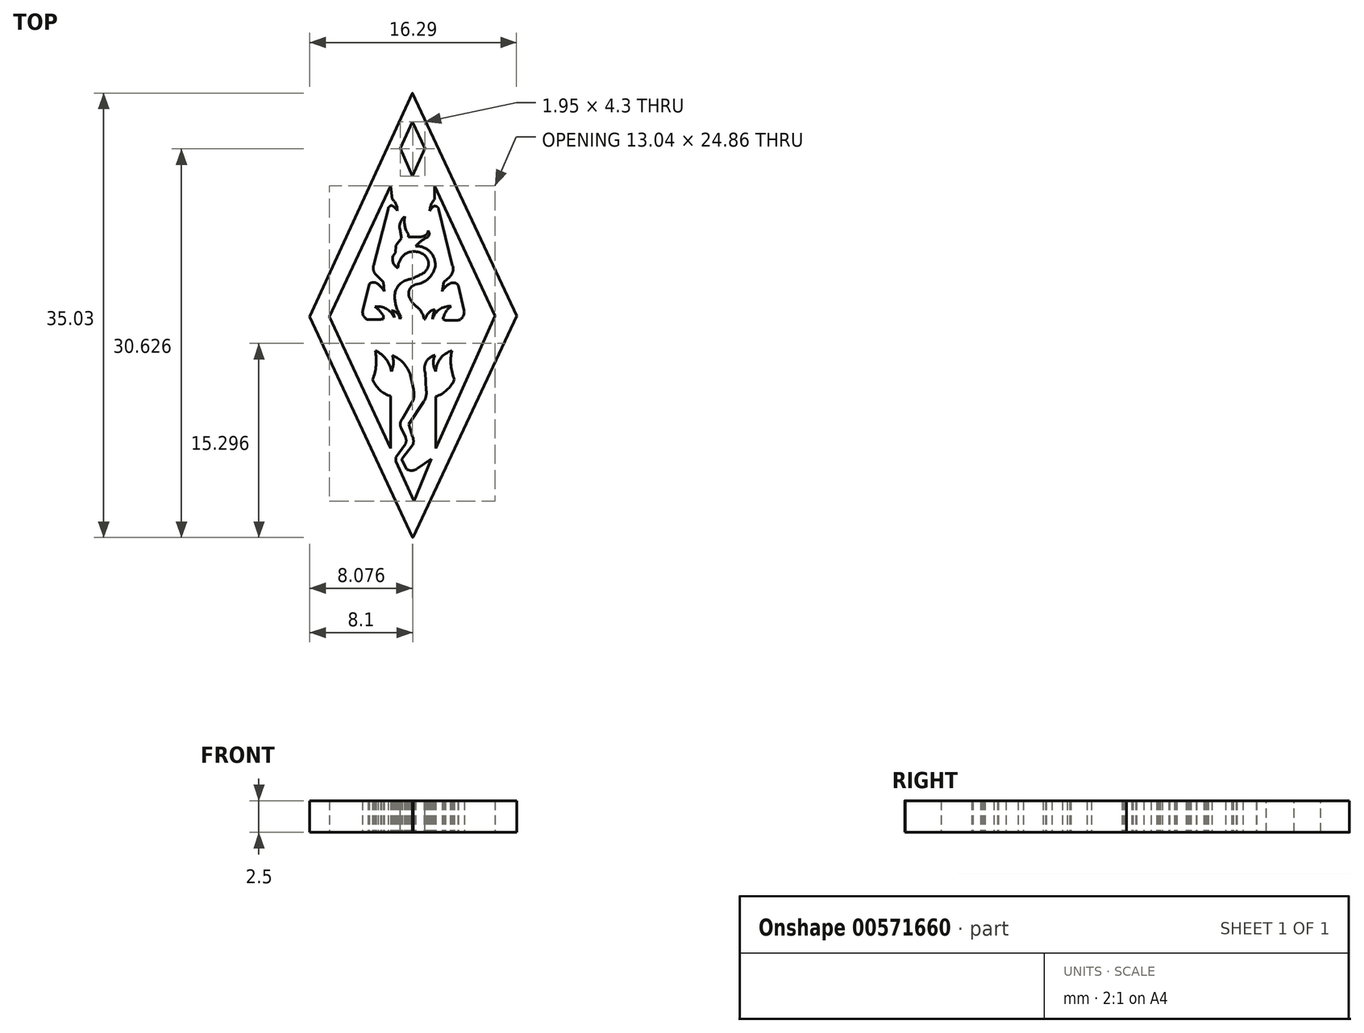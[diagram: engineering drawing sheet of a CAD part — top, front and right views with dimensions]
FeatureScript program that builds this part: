
annotation { "Feature Type Name" : "Feature", "Feature Type Description" : "" }
export const myFeature = defineFeature(function(context is Context, id is Id, definition is map)
    precondition{}
    {
        {
            var Q0;
            Q0=qCreatedBy(makeId("Top.planeOp"),FACE);
            var sketch = newSketch(context, id + "F0", { "sketchPlane" : qUnion([Q0])});
            skPoint(sketch, "E0.endSnap0", {"position": v(12.98, 25.96) * mm});
            skLineSegment(sketch, "E1", {"start": v(14.47, 3.72) * mm, "end": v(13.1, 0.4) * mm});
            skLineSegment(sketch, "E2", {"start": v(13.1, 0.4) * mm, "end": v(11.67, 3.52) * mm});
            skLineSegment(sketch, "E3", {"start": v(14.47, 3.72) * mm, "end": v(13.35, 2.95) * mm});
            skLineSegment(sketch, "E4", {"start": v(12.54, 2.9) * mm, "end": v(12.14, 3.64) * mm});
            skArc(sketch, "E5", {"start": v(12.54, 2.9) * mm, "mid": v(12.95, 2.8) * mm, "end": v(13.35, 2.95) * mm});
            skLineSegment(sketch, "E6", {"start": v(11.67, 3.52) * mm, "end": v(11.67, 3.85) * mm});
            skLineSegment(sketch, "E7", {"start": v(12.14, 3.64) * mm, "end": v(12.14, 3.7) * mm});
            skLineSegment(sketch, "E8", {"start": v(12.14, 3.7) * mm, "end": v(13.02, 4.84) * mm});
            skLineSegment(sketch, "E9", {"start": v(11.67, 3.85) * mm, "end": v(12.44, 4.91) * mm});
            skArc(sketch, "E10", {"start": v(13.02, 4.84) * mm, "mid": v(13.05, 5.18) * mm, "end": v(12.99, 5.51) * mm});
            skLineSegment(sketch, "E11", {"start": v(12.42, 5.44) * mm, "end": v(12.08, 6.18) * mm});
            skArc(sketch, "E12", {"start": v(12.44, 4.91) * mm, "mid": v(12.48, 5.18) * mm, "end": v(12.42, 5.44) * mm});
            skLineSegment(sketch, "E13", {"start": v(12.17, 6.88) * mm, "end": v(13.06, 8.42) * mm});
            skArc(sketch, "E14", {"start": v(12.17, 6.88) * mm, "mid": v(12.02, 6.54) * mm, "end": v(12.08, 6.18) * mm});
            skLineSegment(sketch, "E15", {"start": v(12.99, 5.51) * mm, "end": v(12.68, 6.46) * mm});
            skLineSegment(sketch, "E16", {"start": v(12.68, 6.46) * mm, "end": v(13.87, 8.24) * mm});
            skArc(sketch, "E17", {"start": v(13.87, 8.24) * mm, "mid": v(14.05, 8.66) * mm, "end": v(14.06, 9.12) * mm});
            skArc(sketch, "E18", {"start": v(13.06, 8.42) * mm, "mid": v(13.1, 8.8) * mm, "end": v(13.06, 9.19) * mm});
            skLineSegment(sketch, "E19", {"start": v(13.06, 9.19) * mm, "end": v(12.81, 10.33) * mm});
            skLineSegment(sketch, "E20", {"start": v(14.06, 9.12) * mm, "end": v(13.98, 10.53) * mm});
            skArc(sketch, "E21", {"start": v(12.81, 10.33) * mm, "mid": v(12.28, 11.27) * mm, "end": v(11.39, 11.89) * mm});
            skArc(sketch, "E22", {"start": v(11.3, 10.61) * mm, "mid": v(11.47, 11.24) * mm, "end": v(11.39, 11.89) * mm});
            skArc(sketch, "E23", {"start": v(11.3, 10.61) * mm, "mid": v(10.9, 11.6) * mm, "end": v(10.05, 12.26) * mm});
            skArc(sketch, "E24", {"start": v(9.83, 9.97) * mm, "mid": v(10.1, 11.1) * mm, "end": v(10.05, 12.26) * mm});
            skArc(sketch, "E25", {"start": v(9.83, 9.97) * mm, "mid": v(10.4, 9.15) * mm, "end": v(11.27, 8.67) * mm});
            skLineSegment(sketch, "E26", {"start": v(11.27, 8.67) * mm, "end": v(11.27, 4.55) * mm});
            skLineSegment(sketch, "E27", {"start": v(11.27, 4.55) * mm, "end": v(6.45, 14.94) * mm});
            skLineSegment(sketch, "E28", {"start": v(6.45, 14.94) * mm, "end": v(11.27, 25.26) * mm});
            skLineSegment(sketch, "E29", {"start": v(11.27, 25.26) * mm, "end": v(11.37, 24.33) * mm});
            skLineSegment(sketch, "E30", {"start": v(11.37, 24.33) * mm, "end": v(11.4, 24.19) * mm});
            skArc(sketch, "E31", {"start": v(11.78, 23.27) * mm, "mid": v(11.7, 23.78) * mm, "end": v(11.4, 24.19) * mm});
            skArc(sketch, "E32", {"start": v(11.78, 23.27) * mm, "mid": v(11.6, 23.5) * mm, "end": v(11.4, 23.69) * mm});
            skArc(sketch, "E33", {"start": v(11.4, 23.69) * mm, "mid": v(11.16, 23.62) * mm, "end": v(11.05, 23.4) * mm});
            skLineSegment(sketch, "E34", {"start": v(11.05, 23.4) * mm, "end": v(9.91, 19) * mm});
            skArc(sketch, "E35", {"start": v(9.91, 19) * mm, "mid": v(9.9, 18.66) * mm, "end": v(10.02, 18.34) * mm});
            skLineSegment(sketch, "E36", {"start": v(10.02, 18.34) * mm, "end": v(10.69, 17.66) * mm});
            skLineSegment(sketch, "E37", {"start": v(10.69, 17.66) * mm, "end": v(10.75, 16.94) * mm});
            skArc(sketch, "E38", {"start": v(10.26, 17.5) * mm, "mid": v(9.91, 17.64) * mm, "end": v(9.57, 17.5) * mm});
            skLineSegment(sketch, "E39", {"start": v(9.57, 17.5) * mm, "end": v(9.07, 15.44) * mm});
            skArc(sketch, "E40", {"start": v(9.07, 15.44) * mm, "mid": v(9.13, 14.99) * mm, "end": v(9.47, 14.7) * mm});
            skLineSegment(sketch, "E41", {"start": v(9.47, 14.7) * mm, "end": v(10.46, 14.7) * mm});
            skLineSegment(sketch, "E42", {"start": v(10.46, 14.7) * mm, "end": v(10.53, 14.74) * mm});
            skLineSegment(sketch, "E43", {"start": v(10.53, 14.74) * mm, "end": v(10.67, 14.74) * mm});
            skLineSegment(sketch, "E44", {"start": v(10.67, 14.74) * mm, "end": v(10.67, 15) * mm});
            skArc(sketch, "E45", {"start": v(10.67, 15) * mm, "mid": v(10.39, 15.4) * mm, "end": v(10, 15.72) * mm});
            skArc(sketch, "E46", {"start": v(11.54, 14.88) * mm, "mid": v(10.91, 15.55) * mm, "end": v(10, 15.72) * mm});
            skArc(sketch, "E47", {"start": v(11.54, 14.88) * mm, "mid": v(11.48, 15.16) * mm, "end": v(11.33, 15.41) * mm});
            skArc(sketch, "E48", {"start": v(12, 14.74) * mm, "mid": v(11.79, 15.2) * mm, "end": v(11.33, 15.41) * mm});
            skLineSegment(sketch, "E49", {"start": v(12, 14.74) * mm, "end": v(12.09, 14.95) * mm});
            skArc(sketch, "E50", {"start": v(11.58, 16.55) * mm, "mid": v(11.7, 15.7) * mm, "end": v(12.09, 14.95) * mm});
            skArc(sketch, "E51", {"start": v(12.52, 17.82) * mm, "mid": v(11.84, 17.34) * mm, "end": v(11.58, 16.55) * mm});
            skArc(sketch, "E52", {"start": v(12.52, 17.82) * mm, "mid": v(13.22, 18.06) * mm, "end": v(13.88, 18.4) * mm});
            skArc(sketch, "E53", {"start": v(13.88, 18.4) * mm, "mid": v(14.25, 19.1) * mm, "end": v(13.88, 19.82) * mm});
            skArc(sketch, "E54", {"start": v(13.88, 19.82) * mm, "mid": v(13.1, 20.07) * mm, "end": v(12.32, 19.82) * mm});
            skArc(sketch, "E55", {"start": v(12.32, 19.82) * mm, "mid": v(11.97, 19.35) * mm, "end": v(11.83, 18.78) * mm});
            skArc(sketch, "E56", {"start": v(11.45, 19.71) * mm, "mid": v(11.46, 19.17) * mm, "end": v(11.83, 18.78) * mm});
            skLineSegment(sketch, "E57", {"start": v(11.45, 19.71) * mm, "end": v(11.65, 19.97) * mm});
            skLineSegment(sketch, "E58", {"start": v(11.65, 19.97) * mm, "end": v(11.68, 20.54) * mm});
            skLineSegment(sketch, "E59", {"start": v(11.68, 20.54) * mm, "end": v(12.1, 21.1) * mm});
            skLineSegment(sketch, "E60", {"start": v(12.1, 21.1) * mm, "end": v(11.98, 21.86) * mm});
            skArc(sketch, "E61", {"start": v(12.38, 22.83) * mm, "mid": v(12.04, 22.4) * mm, "end": v(11.98, 21.86) * mm});
            skArc(sketch, "E62", {"start": v(12.38, 22.83) * mm, "mid": v(12.37, 22.11) * mm, "end": v(12.64, 21.45) * mm});
            skLineSegment(sketch, "E63", {"start": v(12.64, 21.45) * mm, "end": v(12.64, 21.23) * mm});
            skLineSegment(sketch, "E64", {"start": v(12.64, 21.23) * mm, "end": v(13.6, 21.23) * mm});
            skArc(sketch, "E65", {"start": v(13.6, 21.23) * mm, "mid": v(13.8, 21.26) * mm, "end": v(14, 21.36) * mm});
            skArc(sketch, "E66", {"start": v(14, 21.36) * mm, "mid": v(14.15, 21.51) * mm, "end": v(14.2, 21.73) * mm});
            skArc(sketch, "E67", {"start": v(14.2, 21.23) * mm, "mid": v(14.3, 21.48) * mm, "end": v(14.2, 21.73) * mm});
            skArc(sketch, "E68", {"start": v(14.2, 21.23) * mm, "mid": v(13.68, 20.9) * mm, "end": v(13.22, 20.5) * mm});
            skArc(sketch, "E69", {"start": v(14.77, 18.92) * mm, "mid": v(14.35, 20.05) * mm, "end": v(13.22, 20.5) * mm});
            skArc(sketch, "E70", {"start": v(13.22, 17.47) * mm, "mid": v(14.24, 17.93) * mm, "end": v(14.77, 18.92) * mm});
            skArc(sketch, "E71", {"start": v(13.22, 17.47) * mm, "mid": v(12.73, 17.02) * mm, "end": v(12.78, 16.36) * mm});
            skArc(sketch, "E72", {"start": v(12.78, 16.36) * mm, "mid": v(12.97, 16.05) * mm, "end": v(13.22, 15.78) * mm});
            skArc(sketch, "E73", {"start": v(13.9, 14.74) * mm, "mid": v(13.67, 15.33) * mm, "end": v(13.22, 15.78) * mm});
            skLineSegment(sketch, "E74", {"start": v(13.9, 14.74) * mm, "end": v(13.98, 14.74) * mm});
            skArc(sketch, "E75", {"start": v(14.75, 15.5) * mm, "mid": v(14.25, 15.24) * mm, "end": v(13.98, 14.74) * mm});
            skArc(sketch, "E76", {"start": v(14.75, 15.5) * mm, "mid": v(14.62, 15.13) * mm, "end": v(14.55, 14.74) * mm});
            skArc(sketch, "E77", {"start": v(16, 15.74) * mm, "mid": v(15.1, 15.5) * mm, "end": v(14.55, 14.74) * mm});
            skArc(sketch, "E78", {"start": v(16, 15.74) * mm, "mid": v(15.6, 15.3) * mm, "end": v(15.39, 14.74) * mm});
            skLineSegment(sketch, "E79", {"start": v(15.39, 14.74) * mm, "end": v(15.56, 14.64) * mm});
            skLineSegment(sketch, "E80", {"start": v(15.56, 14.64) * mm, "end": v(16.56, 14.64) * mm});
            skArc(sketch, "E81", {"start": v(16.56, 14.64) * mm, "mid": v(16.96, 14.94) * mm, "end": v(17.04, 15.44) * mm});
            skLineSegment(sketch, "E82", {"start": v(17.04, 15.44) * mm, "end": v(16.58, 17.38) * mm});
            skArc(sketch, "E83", {"start": v(16.58, 17.38) * mm, "mid": v(16.3, 17.6) * mm, "end": v(15.95, 17.55) * mm});
            skArc(sketch, "E84", {"start": v(15.95, 17.55) * mm, "mid": v(15.58, 17.3) * mm, "end": v(15.3, 16.94) * mm});
            skArc(sketch, "E85", {"start": v(10.75, 16.94) * mm, "mid": v(10.53, 17.25) * mm, "end": v(10.26, 17.5) * mm});
            skLineSegment(sketch, "E86", {"start": v(15.43, 17.66) * mm, "end": v(15.3, 16.94) * mm});
            skLineSegment(sketch, "E87", {"start": v(15.43, 17.66) * mm, "end": v(15.91, 18.09) * mm});
            skArc(sketch, "E88", {"start": v(15.91, 18.09) * mm, "mid": v(16.16, 18.5) * mm, "end": v(16.13, 18.98) * mm});
            skLineSegment(sketch, "E89", {"start": v(16.13, 18.98) * mm, "end": v(15.05, 23.4) * mm});
            skArc(sketch, "E90", {"start": v(15.05, 23.4) * mm, "mid": v(14.88, 23.62) * mm, "end": v(14.61, 23.62) * mm});
            skPoint(sketch, "E90.endSnap0", {"position": v(11.16, 23.62) * mm});
            skArc(sketch, "E91", {"start": v(14.61, 23.62) * mm, "mid": v(14.47, 23.46) * mm, "end": v(14.35, 23.27) * mm});
            skArc(sketch, "E92", {"start": v(14.7, 24.19) * mm, "mid": v(14.45, 23.76) * mm, "end": v(14.35, 23.27) * mm});
            skLineSegment(sketch, "E93", {"start": v(14.7, 24.19) * mm, "end": v(14.7, 25.24) * mm});
            skLineSegment(sketch, "E94", {"start": v(14.7, 25.24) * mm, "end": v(19.49, 15) * mm});
            skLineSegment(sketch, "E95", {"start": v(19.49, 15) * mm, "end": v(14.81, 4.55) * mm});
            skLineSegment(sketch, "E96", {"start": v(14.81, 4.55) * mm, "end": v(14.81, 8.64) * mm});
            skArc(sketch, "E97", {"start": v(14.81, 8.64) * mm, "mid": v(15.69, 9.15) * mm, "end": v(16.28, 9.97) * mm});
            skArc(sketch, "E98", {"start": v(16.08, 12.26) * mm, "mid": v(16, 11.1) * mm, "end": v(16.28, 9.97) * mm});
            skArc(sketch, "E99", {"start": v(16.08, 12.26) * mm, "mid": v(15.18, 11.64) * mm, "end": v(14.81, 10.61) * mm});
            skArc(sketch, "E100", {"start": v(14.74, 11.89) * mm, "mid": v(14.63, 11.24) * mm, "end": v(14.81, 10.61) * mm});
            skArc(sketch, "E101", {"start": v(14.74, 11.89) * mm, "mid": v(14.06, 11.38) * mm, "end": v(13.98, 10.53) * mm});
            skPoint(sketch, "E102", {"position": v(12.98, 32.56) * mm});
            skArc(sketch, "E103", {"start": v(12.98, 32.56) * mm, "mid": v(12.98, 32.56) * mm, "end": v(12.98, 32.56) * mm});
            skLineSegment(sketch, "E104", {"start": v(12.98, 32.56) * mm, "end": v(4.89, 14.94) * mm});
            skLineSegment(sketch, "E105", {"start": v(12.98, 32.56) * mm, "end": v(21.18, 15) * mm});
            skPoint(sketch, "E106", {"position": v(12.96, -2.44) * mm});
            skPoint(sketch, "E107", {"position": v(13.02, -2.44) * mm});
            skArc(sketch, "E108", {"start": v(12.96, -2.44) * mm, "mid": v(13, -2.47) * mm, "end": v(13.02, -2.44) * mm});
            skLineSegment(sketch, "E109", {"start": v(12.96, -2.44) * mm, "end": v(4.89, 14.94) * mm});
            skLineSegment(sketch, "E110", {"start": v(13.02, -2.44) * mm, "end": v(21.18, 15) * mm});
            skSolve(sketch);
        }
        {
            var Q0;
            Q0=makeQuery(id+"F0.imprint","IMPRINT",FACE,{"disambiguationData":[TD([[makeQuery(id+"F0.imprint","IMPRINT",EDGE,{"derivedFrom":sQuery(id+"F0.wireOp",EDGE,"E1")}),1.0]])]});
            extrude(context, id + "F1", {"entities" : qUnion([Q0]), "depth" : 2.5 * mm, "offsetDistance" : 25 * mm});
        }
        {
            var Q0;
            Q0=makeQuery(id+"F1.opExtrude","CAP_FACE",FACE,{"disambiguationData":[OSD([sQuery(id+"F0.wireOp",EDGE,"td3pEOfP-NWMg-dh41-Z3LD-Hokq7qkz871T"),sQuery(id+"F0.wireOp",EDGE,"FzXfX3x3-jCT8-vBJj-UMJg-uvLs6Eh42bVe"),sQuery(id+"F0.wireOp",EDGE,"E0"),sQuery(id+"F0.wireOp",EDGE,"AmwVXDHx-6MG1-58SC-kDPZ-zLn1lo49yHkA"),sQuery(id+"F0.wireOp",EDGE,"E1"),sQuery(id+"F0.wireOp",EDGE,"E2"),sQuery(id+"F0.wireOp",EDGE,"E3"),sQuery(id+"F0.wireOp",EDGE,"E4"),sQuery(id+"F0.wireOp",EDGE,"E5"),sQuery(id+"F0.wireOp",EDGE,"E6"),sQuery(id+"F0.wireOp",EDGE,"E7"),sQuery(id+"F0.wireOp",EDGE,"E8"),sQuery(id+"F0.wireOp",EDGE,"E9"),sQuery(id+"F0.wireOp",EDGE,"E10"),sQuery(id+"F0.wireOp",EDGE,"E11"),sQuery(id+"F0.wireOp",EDGE,"E12"),sQuery(id+"F0.wireOp",EDGE,"E13"),sQuery(id+"F0.wireOp",EDGE,"E14"),sQuery(id+"F0.wireOp",EDGE,"E15"),sQuery(id+"F0.wireOp",EDGE,"E16"),sQuery(id+"F0.wireOp",EDGE,"E17"),sQuery(id+"F0.wireOp",EDGE,"E18"),sQuery(id+"F0.wireOp",EDGE,"E19"),sQuery(id+"F0.wireOp",EDGE,"E20"),sQuery(id+"F0.wireOp",EDGE,"E21"),sQuery(id+"F0.wireOp",EDGE,"E22"),sQuery(id+"F0.wireOp",EDGE,"E23"),sQuery(id+"F0.wireOp",EDGE,"E24"),sQuery(id+"F0.wireOp",EDGE,"E25"),sQuery(id+"F0.wireOp",EDGE,"E26"),sQuery(id+"F0.wireOp",EDGE,"E27"),sQuery(id+"F0.wireOp",EDGE,"E28"),sQuery(id+"F0.wireOp",EDGE,"E29"),sQuery(id+"F0.wireOp",EDGE,"E30"),sQuery(id+"F0.wireOp",EDGE,"E31"),sQuery(id+"F0.wireOp",EDGE,"E32"),sQuery(id+"F0.wireOp",EDGE,"E33"),sQuery(id+"F0.wireOp",EDGE,"E34"),sQuery(id+"F0.wireOp",EDGE,"E35"),sQuery(id+"F0.wireOp",EDGE,"E36"),sQuery(id+"F0.wireOp",EDGE,"E37"),sQuery(id+"F0.wireOp",EDGE,"E38"),sQuery(id+"F0.wireOp",EDGE,"E39"),sQuery(id+"F0.wireOp",EDGE,"E40"),sQuery(id+"F0.wireOp",EDGE,"E41"),sQuery(id+"F0.wireOp",EDGE,"E42"),sQuery(id+"F0.wireOp",EDGE,"E43"),sQuery(id+"F0.wireOp",EDGE,"E44"),sQuery(id+"F0.wireOp",EDGE,"E45"),sQuery(id+"F0.wireOp",EDGE,"E46"),sQuery(id+"F0.wireOp",EDGE,"E47"),sQuery(id+"F0.wireOp",EDGE,"E48"),sQuery(id+"F0.wireOp",EDGE,"E49"),sQuery(id+"F0.wireOp",EDGE,"E50"),sQuery(id+"F0.wireOp",EDGE,"E51"),sQuery(id+"F0.wireOp",EDGE,"E52"),sQuery(id+"F0.wireOp",EDGE,"E53"),sQuery(id+"F0.wireOp",EDGE,"E54"),sQuery(id+"F0.wireOp",EDGE,"E55"),sQuery(id+"F0.wireOp",EDGE,"E56"),sQuery(id+"F0.wireOp",EDGE,"E57"),sQuery(id+"F0.wireOp",EDGE,"E58"),sQuery(id+"F0.wireOp",EDGE,"E59"),sQuery(id+"F0.wireOp",EDGE,"E60"),sQuery(id+"F0.wireOp",EDGE,"E61"),sQuery(id+"F0.wireOp",EDGE,"E62"),sQuery(id+"F0.wireOp",EDGE,"E63"),sQuery(id+"F0.wireOp",EDGE,"E64"),sQuery(id+"F0.wireOp",EDGE,"E65"),sQuery(id+"F0.wireOp",EDGE,"E66"),sQuery(id+"F0.wireOp",EDGE,"E67"),sQuery(id+"F0.wireOp",EDGE,"E68"),sQuery(id+"F0.wireOp",EDGE,"E69"),sQuery(id+"F0.wireOp",EDGE,"E70"),sQuery(id+"F0.wireOp",EDGE,"E71"),sQuery(id+"F0.wireOp",EDGE,"E72"),sQuery(id+"F0.wireOp",EDGE,"E73"),sQuery(id+"F0.wireOp",EDGE,"E74"),sQuery(id+"F0.wireOp",EDGE,"E75"),sQuery(id+"F0.wireOp",EDGE,"E76"),sQuery(id+"F0.wireOp",EDGE,"E77"),sQuery(id+"F0.wireOp",EDGE,"E78"),sQuery(id+"F0.wireOp",EDGE,"E79"),sQuery(id+"F0.wireOp",EDGE,"E80"),sQuery(id+"F0.wireOp",EDGE,"E81"),sQuery(id+"F0.wireOp",EDGE,"E82"),sQuery(id+"F0.wireOp",EDGE,"E83"),sQuery(id+"F0.wireOp",EDGE,"E84"),sQuery(id+"F0.wireOp",EDGE,"E85"),sQuery(id+"F0.wireOp",EDGE,"E86"),sQuery(id+"F0.wireOp",EDGE,"E87"),sQuery(id+"F0.wireOp",EDGE,"E88"),sQuery(id+"F0.wireOp",EDGE,"E89"),sQuery(id+"F0.wireOp",EDGE,"E90"),sQuery(id+"F0.wireOp",EDGE,"E91"),sQuery(id+"F0.wireOp",EDGE,"E92"),sQuery(id+"F0.wireOp",EDGE,"E93"),sQuery(id+"F0.wireOp",EDGE,"E94"),sQuery(id+"F0.wireOp",EDGE,"E95"),sQuery(id+"F0.wireOp",EDGE,"E96"),sQuery(id+"F0.wireOp",EDGE,"E97"),sQuery(id+"F0.wireOp",EDGE,"E98"),sQuery(id+"F0.wireOp",EDGE,"E99"),sQuery(id+"F0.wireOp",EDGE,"E100"),sQuery(id+"F0.wireOp",EDGE,"E101")])],"isStart":false});
            var sketch = newSketch(context, id + "F2", { "sketchPlane" : qUnion([Q0])});
            skLineSegment(sketch, "E111", {"start": v(12.98, 30.3) * mm, "end": v(12.01, 28.2) * mm});
            skLineSegment(sketch, "E112", {"start": v(12.01, 28.2) * mm, "end": v(12.96, 26) * mm});
            skLineSegment(sketch, "E113", {"start": v(12.96, 26) * mm, "end": v(13.97, 28.2) * mm});
            skLineSegment(sketch, "E114", {"start": v(13.97, 28.2) * mm, "end": v(12.98, 30.3) * mm});
            skSolve(sketch);
        }
        {
            var Q0;
            Q0 = qSketchRegion(id + "F2", true);
            extrude(context, id + "F3", {"entities" : qUnion([Q0]), "operationType" : NewBodyOperationType.REMOVE, "oppositeDirection" : true, "depth" : 25 * mm, "offsetDistance" : 25 * mm});
        }
    });
